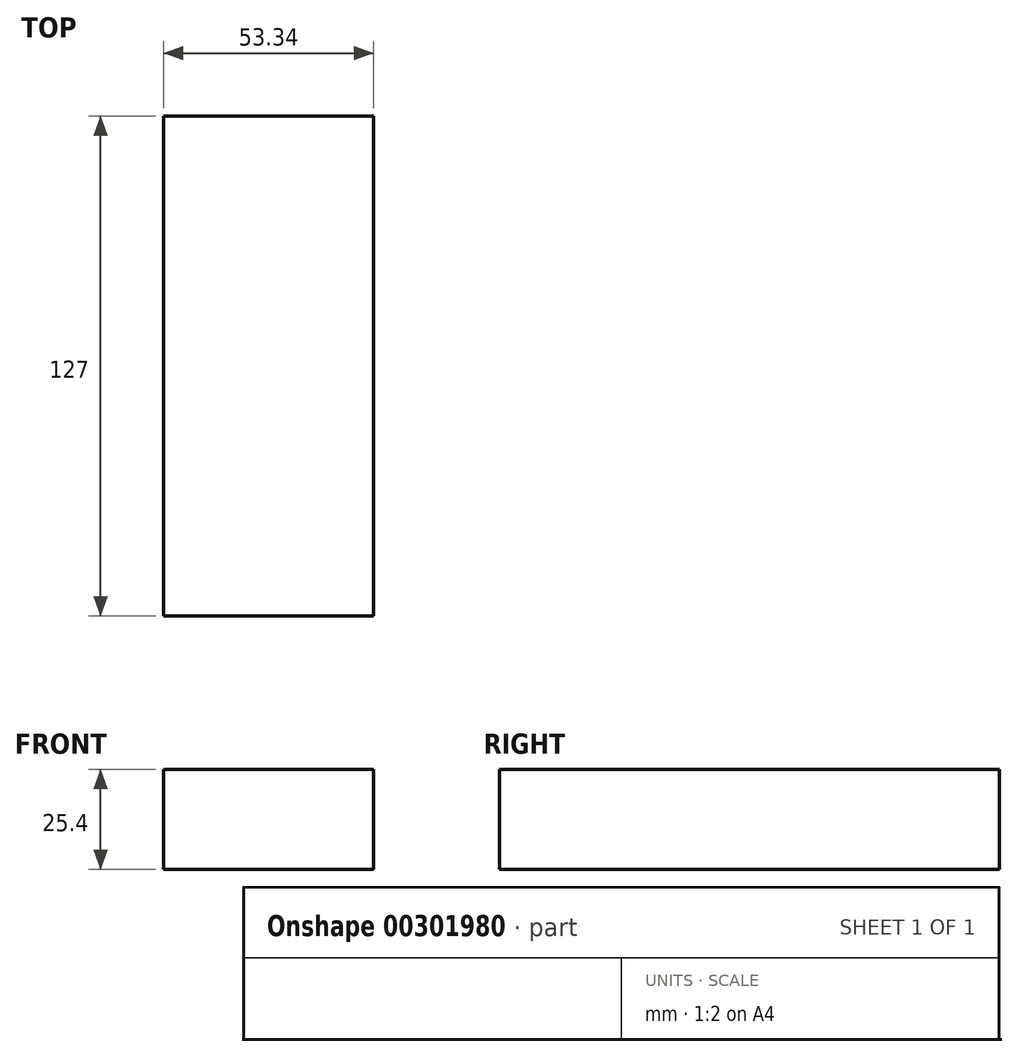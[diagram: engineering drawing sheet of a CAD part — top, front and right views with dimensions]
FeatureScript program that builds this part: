
annotation { "Feature Type Name" : "Feature", "Feature Type Description" : "" }
export const myFeature = defineFeature(function(context is Context, id is Id, definition is map)
    precondition{}
    {
        {
            var Q0;
            Q0=qCreatedBy(makeId("Front.planeOp"),FACE);
            var sketch = newSketch(context, id + "F0", { "sketchPlane" : qUnion([Q0])});
            skLineSegment(sketch, "E0.bottom", {"start": v(-45.72, 0) * mm, "end": v(7.62, 0) * mm});
            skLineSegment(sketch, "E0.top", {"start": v(-45.72, -25.4) * mm, "end": v(7.62, -25.4) * mm});
            skLineSegment(sketch, "E0.left", {"start": v(-45.72, 0) * mm, "end": v(-45.72, -25.4) * mm});
            skLineSegment(sketch, "E0.right", {"start": v(7.62, 0) * mm, "end": v(7.62, -25.4) * mm});
            skSolve(sketch);
        }
        {
            var Q0;
            Q0 = qSketchRegion(id + "F0", true);
            extrude(context, id + "F1", {"entities" : qUnion([Q0]), "endBound" : BoundingType.SYMMETRIC, "depth" : 127 * mm});
        }
    });
